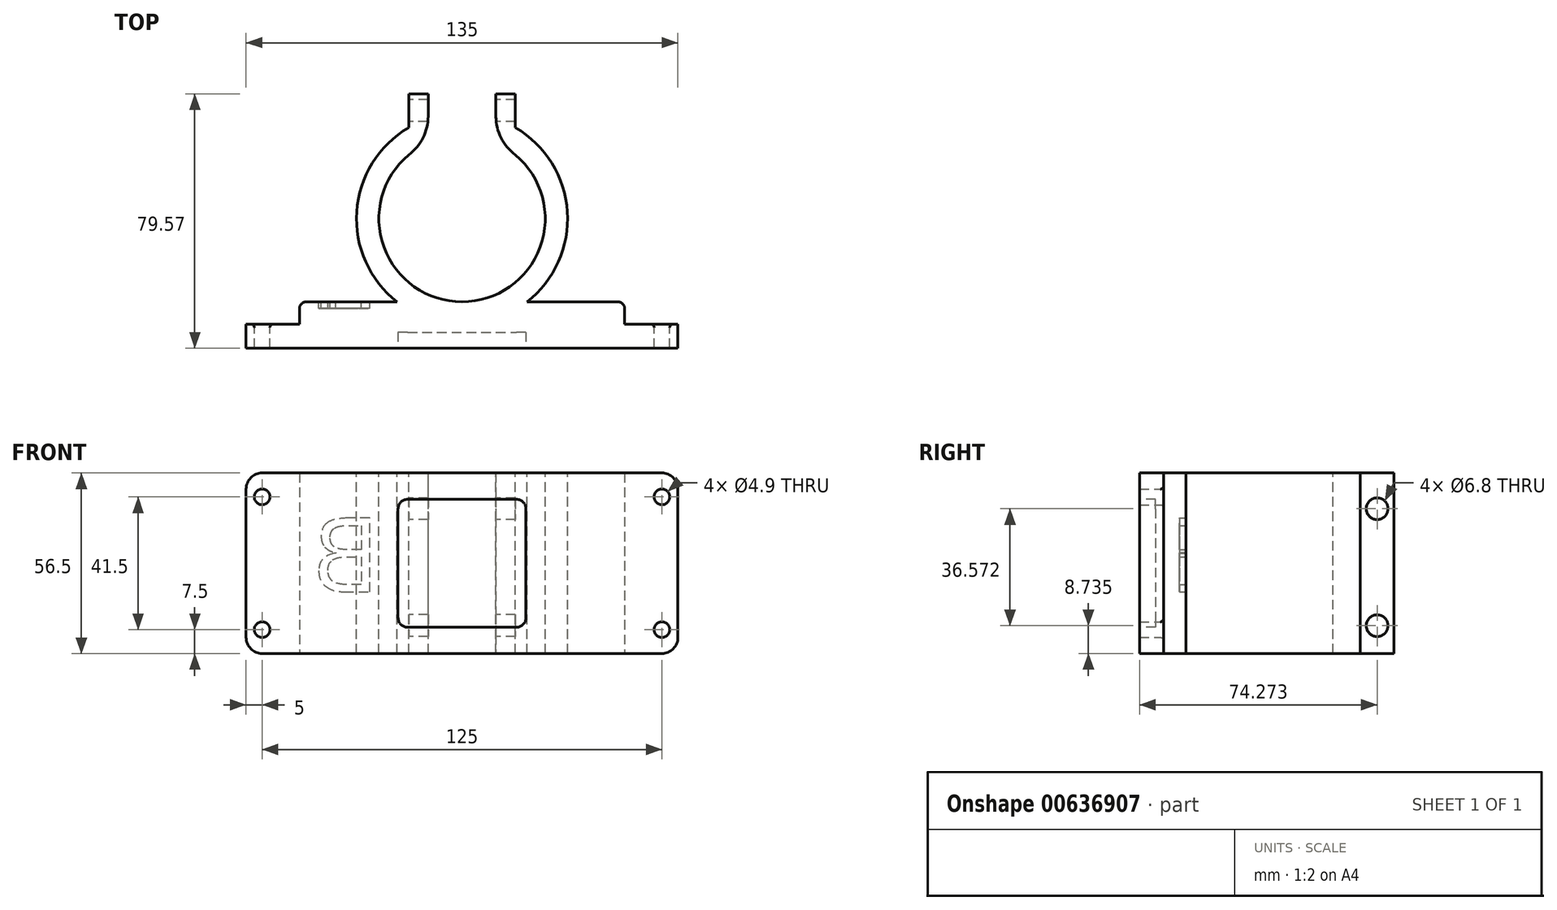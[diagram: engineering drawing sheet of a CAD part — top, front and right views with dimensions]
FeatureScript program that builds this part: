
annotation { "Feature Type Name" : "Feature", "Feature Type Description" : "" }
export const myFeature = defineFeature(function(context is Context, id is Id, definition is map)
    precondition{}
    {
        {
            var Q0;
            Q0=qCreatedBy(makeId("Front.planeOp"),FACE);
            var sketch = newSketch(context, id + "F0", { "sketchPlane" : qUnion([Q0])});
            skLineSegment(sketch, "E0.bottom", {"start": v(67.5, -28.25) * mm, "end": v(-67.5, -28.25) * mm});
            skLineSegment(sketch, "E0.top", {"start": v(67.5, 28.25) * mm, "end": v(-67.5, 28.25) * mm});
            skLineSegment(sketch, "E0.left", {"start": v(67.5, -28.25) * mm, "end": v(67.5, 28.25) * mm});
            skLineSegment(sketch, "E0.right", {"start": v(-67.5, -28.25) * mm, "end": v(-67.5, 28.25) * mm});
            skPoint(sketch, "E0.middle", {"position": v(0, 0) * mm});
            skCircle(sketch, "E1", {"center": v(-62.5, 20.75) * mm, "radius": 2.45 * mm});
            skCircle(sketch, "E2", {"center": v(-62.5, -20.75) * mm, "radius": 2.45 * mm});
            skCircle(sketch, "E3", {"center": v(62.5, 20.75) * mm, "radius": 2.45 * mm});
            skCircle(sketch, "E4", {"center": v(62.5, -20.75) * mm, "radius": 2.45 * mm});
            skLineSegment(sketch, "E5", {"start": v(-62.5, 20.75) * mm, "end": v(-62.5, -20.75) * mm});
            skLineSegment(sketch, "E6", {"start": v(-62.5, -20.75) * mm, "end": v(62.5, -20.75) * mm});
            skLineSegment(sketch, "E7", {"start": v(62.5, -20.75) * mm, "end": v(62.5, 20.75) * mm});
            skLineSegment(sketch, "E8", {"start": v(-62.5, 20.75) * mm, "end": v(62.5, 20.75) * mm});
            skLineSegment(sketch, "E9", {"start": v(-62.5, 20.75) * mm, "end": v(-62.5, 28.25) * mm});
            skLineSegment(sketch, "E10", {"start": v(-62.5, -20.75) * mm, "end": v(-62.5, -28.25) * mm});
            skLineSegment(sketch, "E11", {"start": v(62.5, 20.75) * mm, "end": v(67.5, 20.75) * mm});
            skLineSegment(sketch, "E12", {"start": v(-62.5, 20.75) * mm, "end": v(-67.5, 20.75) * mm});
            skSolve(sketch);
        }
        {
            var Q0;
            {var subQ9=sQuery(id+"F0.wireOp",EDGE,"E0.left");var subQ11=sQuery(id+"F0.wireOp",EDGE,"E0.top");var subQ12=makeQuery(id+"F0.imprint","INTERSECT",VERTEX,{"derivedFrom":[subQ11,subQ9]});Q0=makeQuery(id+"F0.imprint","IMPRINT",FACE,{"disambiguationData":[TD([[makeQuery(id+"F0.imprint","IMPRINT",EDGE,{"disambiguationData":[TD([[subQ12,-1.0]])],"derivedFrom":subQ11}),1.0]])]});}
            var Q1;
            {var subQ5=sQuery(id+"F0.wireOp",EDGE,"E0.right");var subQ6=sQuery(id+"F0.wireOp",EDGE,"E0.top");var subQ7=makeQuery(id+"F0.imprint","INTERSECT",VERTEX,{"derivedFrom":[subQ6,subQ5]});Q1=makeQuery(id+"F0.imprint","IMPRINT",FACE,{"disambiguationData":[TD([[makeQuery(id+"F0.imprint","IMPRINT",EDGE,{"disambiguationData":[TD([[subQ7,1.0]])],"derivedFrom":subQ6}),1.0]])]});}
            var Q2;
            {var subQ5=sQuery(id+"F0.wireOp",EDGE,"E0.bottom");var subQ11=sQuery(id+"F0.wireOp",EDGE,"E0.right");var subQ12=makeQuery(id+"F0.imprint","INTERSECT",VERTEX,{"derivedFrom":[subQ5,subQ11]});Q2=makeQuery(id+"F0.imprint","IMPRINT",FACE,{"disambiguationData":[TD([[makeQuery(id+"F0.imprint","IMPRINT",EDGE,{"disambiguationData":[TD([[subQ12,1.0]])],"derivedFrom":subQ5}),-1.0]])]});}
            var Q3;
            {var subQ9=sQuery(id+"F0.wireOp",EDGE,"E8");var subQ13=sQuery(id+"F0.wireOp",EDGE,"E1");var subQ14=makeQuery(id+"F0.imprint","INTERSECT",VERTEX,{"derivedFrom":[subQ13,subQ9]});Q3=makeQuery(id+"F0.imprint","IMPRINT",FACE,{"disambiguationData":[TD([[makeQuery(id+"F0.imprint","IMPRINT",EDGE,{"disambiguationData":[TD([[subQ14,1.0]])],"derivedFrom":subQ13}),-1.0]])]});}
            var Q4;
            {var subQ10=sQuery(id+"F0.wireOp",EDGE,"E0.left");var subQ11=sQuery(id+"F0.wireOp",EDGE,"E0.bottom");var subQ12=makeQuery(id+"F0.imprint","INTERSECT",VERTEX,{"derivedFrom":[subQ11,subQ10]});Q4=makeQuery(id+"F0.imprint","IMPRINT",FACE,{"disambiguationData":[TD([[makeQuery(id+"F0.imprint","IMPRINT",EDGE,{"disambiguationData":[TD([[subQ12,-1.0]])],"derivedFrom":subQ11}),-1.0]])]});}
            extrude(context, id + "F1", {"entities" : qUnion([Q0, Q1, Q2, Q3, Q4]), "depth" : 7.5 * mm, "offsetDistance" : 25.4 * mm});
        }
        {
            var Q0;
            Q0=makeQuery(id+"F1.opExtrude","SWEPT_EDGE",EDGE,{"disambiguationData":[OSD([sQuery(id+"F0.wireOp",EDGE,"E0.top"),sQuery(id+"F0.wireOp",EDGE,"E0.left")])]});
            var Q1;
            Q1=makeQuery(id+"F1.opExtrude","SWEPT_EDGE",EDGE,{"disambiguationData":[OSD([sQuery(id+"F0.wireOp",EDGE,"E0.bottom"),sQuery(id+"F0.wireOp",EDGE,"E0.left")])]});
            var Q2;
            Q2=makeQuery(id+"F1.opExtrude","SWEPT_EDGE",EDGE,{"disambiguationData":[OSD([sQuery(id+"F0.wireOp",EDGE,"E0.bottom"),sQuery(id+"F0.wireOp",EDGE,"E0.right")])]});
            var Q3;
            Q3=makeQuery(id+"F1.opExtrude","SWEPT_EDGE",EDGE,{"disambiguationData":[OSD([sQuery(id+"F0.wireOp",EDGE,"E0.top"),sQuery(id+"F0.wireOp",EDGE,"E0.right")])]});
            fillet(context, id + "F2", {"entities" : qUnion([Q0, Q1, Q2, Q3]), "radius" : 5.08 * mm, "tangentPropagation" : true, "allowEdgeOverflow" : false});
        }
        {
            var Q0;
            Q0=makeQuery(id+"F1.opExtrude","SWEPT_FACE",FACE,{"disambiguationData":[OSD([sQuery(id+"F0.wireOp",EDGE,"E0.top")])]});
            var sketch = newSketch(context, id + "F3", { "sketchPlane" : qUnion([Q0])});
            skArc(sketch, "E13", {"start": v(-16.68, 52.94) * mm, "mid": v(0, 7) * mm, "end": v(16.68, 52.94) * mm});
            skArc(sketch, "E14", {"start": v(-16.68, 61.47) * mm, "mid": v(0, 0) * mm, "end": v(16.68, 61.47) * mm});
            skLineSegment(sketch, "E15.left", {"start": v(16.68, 52.94) * mm, "end": v(16.68, 72.07) * mm});
            skLineSegment(sketch, "E15.right", {"start": v(-16.68, 52.94) * mm, "end": v(-16.68, 72.07) * mm});
            skPoint(sketch, "E15.middle", {"position": v(0, 59) * mm});
            skPoint(sketch, "E15.bottom.end.orphan", {"position": v(-16.68, 45.93) * mm});
            skPoint(sketch, "E16.orphan", {"position": v(16.68, 45.93) * mm});
            skLineSegment(sketch, "E17", {"start": v(-16.68, 72.07) * mm, "end": v(-10.6, 72.07) * mm});
            skLineSegment(sketch, "E18", {"start": v(-10.6, 72.07) * mm, "end": v(-10.6, 52.94) * mm});
            skLineSegment(sketch, "E19", {"start": v(-10.6, 52.94) * mm, "end": v(-16.68, 52.94) * mm});
            skLineSegment(sketch, "E20", {"start": v(16.68, 72.07) * mm, "end": v(10.6, 72.07) * mm});
            skLineSegment(sketch, "E21", {"start": v(10.6, 72.07) * mm, "end": v(10.6, 52.94) * mm});
            skLineSegment(sketch, "E22", {"start": v(10.6, 52.94) * mm, "end": v(16.68, 52.94) * mm});
            skSolve(sketch);
        }
        {
            var Q0;
            Q0 = qSketchRegion(id + "F3", true);
            extrude(context, id + "F4", {"entities" : qUnion([Q0]), "oppositeDirection" : true, "depth" : 56.5 * mm, "offsetDistance" : 25.4 * mm});
        }
        {
            var Q0;
            Q0=makeQuery(id+"F4.opExtrude","SWEPT_EDGE",EDGE,{"disambiguationData":[OSD([sQuery(id+"F3.wireOp",EDGE,"E18"),sQuery(id+"F3.wireOp",EDGE,"E19")])]});
            var Q1;
            Q1=makeQuery(id+"F4.opExtrude","SWEPT_EDGE",EDGE,{"disambiguationData":[OSD([sQuery(id+"F3.wireOp",EDGE,"E21"),sQuery(id+"F3.wireOp",EDGE,"E22")])]});
            fillet(context, id + "F5", {"entities" : qUnion([Q0, Q1]), "radius" : 15 * mm, "tangentPropagation" : true, "allowEdgeOverflow" : false});
        }
        {
            var Q0;
            Q0=makeQuery(id+"F4.opExtrude","SWEPT_FACE",FACE,{"disambiguationData":[OSD([sQuery(id+"F3.wireOp",EDGE,"E15.right")])]});
            var sketch = newSketch(context, id + "F6", { "sketchPlane" : qUnion([Q0])});
            skCircle(sketch, "E23", {"center": v(-66.77, -19.51) * mm, "radius": 3.4 * mm});
            skCircle(sketch, "E24", {"center": v(-66.77, 17.06) * mm, "radius": 3.4 * mm});
            skPoint(sketch, "E24.centerSnap0", {"position": v(-66.77, 28.25) * mm});
            skLineSegment(sketch, "E25", {"start": v(-66.77, -19.51) * mm, "end": v(-66.77, 17.06) * mm});
            skSolve(sketch);
        }
        {
            var Q0;
            Q0=makeQuery(id+"F6.imprint","IMPRINT",FACE,{"disambiguationData":[TD([[makeQuery(id+"F6.imprint","IMPRINT",EDGE,{"derivedFrom":sQuery(id+"F6.wireOp",EDGE,"E23")}),1.0]])]});
            var Q1;
            Q1=makeQuery(id+"F6.imprint","IMPRINT",FACE,{"disambiguationData":[TD([[makeQuery(id+"F6.imprint","IMPRINT",EDGE,{"derivedFrom":sQuery(id+"F6.wireOp",EDGE,"E24")}),1.0]])]});
            extrude(context, id + "F7", {"entities" : qUnion([Q0, Q1]), "operationType" : NewBodyOperationType.REMOVE, "oppositeDirection" : true, "depth" : 37.85 * mm, "offsetDistance" : 25.4 * mm});
        }
        {
            var Q0;
            Q0=makeQuery(id+"F1.opExtrude","SWEPT_FACE",FACE,{"disambiguationData":[OSD([sQuery(id+"F0.wireOp",EDGE,"E0.bottom")])]});
            var sketch = newSketch(context, id + "F8", { "sketchPlane" : qUnion([Q0])});
            skLineSegment(sketch, "E26.bottom", {"start": v(-50.8, 0) * mm, "end": v(50.8, 0) * mm});
            skLineSegment(sketch, "E26.top", {"start": v(-50.8, -7) * mm, "end": v(50.8, -7) * mm});
            skLineSegment(sketch, "E26.left", {"start": v(-50.8, 0) * mm, "end": v(-50.8, -7) * mm});
            skLineSegment(sketch, "E26.right", {"start": v(50.8, 0) * mm, "end": v(50.8, -7) * mm});
            skLineSegment(sketch, "E27", {"start": v(-62.42, 0) * mm, "end": v(-50.8, 0) * mm});
            skLineSegment(sketch, "E28", {"start": v(50.8, 0) * mm, "end": v(62.42, 0) * mm});
            skSolve(sketch);
        }
        {
            var Q0;
            Q0=makeQuery(id+"F8.imprint","IMPRINT",FACE,{"disambiguationData":[TD([[makeQuery(id+"F8.imprint","IMPRINT",EDGE,{"derivedFrom":sQuery(id+"F8.wireOp",EDGE,"E26.bottom")}),1.0]])]});
            extrude(context, id + "F9", {"entities" : qUnion([Q0]), "operationType" : NewBodyOperationType.ADD, "oppositeDirection" : true, "depth" : 56.5 * mm, "offsetDistance" : 25.4 * mm});
        }
        {
            var Q0;
            Q0=makeQuery(id+"F9.opExtrude","SWEPT_EDGE",EDGE,{"disambiguationData":[OSD([sQuery(id+"F8.wireOp",EDGE,"E26.top"),sQuery(id+"F8.wireOp",EDGE,"E26.left")])]});
            var Q1;
            Q1=makeQuery(id+"F9.opExtrude","SWEPT_EDGE",EDGE,{"disambiguationData":[OSD([sQuery(id+"F8.wireOp",EDGE,"E26.top"),sQuery(id+"F8.wireOp",EDGE,"E26.right")])]});
            fillet(context, id + "F10", {"entities" : qUnion([Q0, Q1]), "radius" : 2 * mm, "tangentPropagation" : true, "allowEdgeOverflow" : false});
        }
        {
            var Q0;
            Q0=makeQuery(id+"F1.opExtrude","CAP_FACE",FACE,{"disambiguationData":[OSD([sQuery(id+"F0.wireOp",EDGE,"E0.bottom"),sQuery(id+"F0.wireOp",EDGE,"E0.top"),sQuery(id+"F0.wireOp",EDGE,"E0.left"),sQuery(id+"F0.wireOp",EDGE,"E0.right"),sQuery(id+"F0.wireOp",EDGE,"E1"),sQuery(id+"F0.wireOp",EDGE,"E2"),sQuery(id+"F0.wireOp",EDGE,"E3"),sQuery(id+"F0.wireOp",EDGE,"E4")])],"isStart":false});
            var sketch = newSketch(context, id + "F11", { "sketchPlane" : qUnion([Q0])});
            skLineSegment(sketch, "E29.bottom", {"start": v(-17, 20) * mm, "end": v(17, 20) * mm});
            skLineSegment(sketch, "E29.top", {"start": v(-17, -20) * mm, "end": v(17, -20) * mm});
            skLineSegment(sketch, "E29.left", {"start": v(-20, 17) * mm, "end": v(-20, -17) * mm});
            skLineSegment(sketch, "E29.right", {"start": v(20, 17) * mm, "end": v(20, -17) * mm});
            skPoint(sketch, "E29.middle", {"position": v(0, 0) * mm});
            skPoint(sketch, "E30.visualSharp", {"position": v(-20, 20) * mm});
            skArc(sketch, "E30.filletArc", {"start": v(-17, 20) * mm, "mid": v(-19.12, 19.12) * mm, "end": v(-20, 17) * mm});
            skPoint(sketch, "E31.visualSharp", {"position": v(20, 20) * mm});
            skArc(sketch, "E31.filletArc", {"start": v(20, 17) * mm, "mid": v(19.12, 19.12) * mm, "end": v(17, 20) * mm});
            skPoint(sketch, "E32.visualSharp", {"position": v(20, -20) * mm});
            skArc(sketch, "E32.filletArc", {"start": v(17, -20) * mm, "mid": v(19.12, -19.12) * mm, "end": v(20, -17) * mm});
            skPoint(sketch, "E33.visualSharp", {"position": v(-20, -20) * mm});
            skArc(sketch, "E33.filletArc", {"start": v(-20, -17) * mm, "mid": v(-19.12, -19.12) * mm, "end": v(-17, -20) * mm});
            skSolve(sketch);
        }
        {
            var Q0;
            Q0=makeQuery(id+"F11.imprint","IMPRINT",FACE,{"disambiguationData":[TD([[makeQuery(id+"F11.imprint","IMPRINT",EDGE,{"derivedFrom":sQuery(id+"F11.wireOp",EDGE,"E29.bottom")}),-1.0]])]});
            extrude(context, id + "F12", {"entities" : qUnion([Q0]), "operationType" : NewBodyOperationType.REMOVE, "oppositeDirection" : true, "depth" : 5 * mm, "offsetDistance" : 25.4 * mm});
        }
        {
            var Q0;
            Q0=makeQuery(id+"F1.opExtrude","CAP_EDGE",EDGE,{"disambiguationData":[OSD([sQuery(id+"F0.wireOp",EDGE,"E2")])],"isStart":true});
            var Q1;
            Q1=makeQuery(id+"F1.opExtrude","CAP_EDGE",EDGE,{"disambiguationData":[OSD([sQuery(id+"F0.wireOp",EDGE,"E1")])],"isStart":true});
            var Q2;
            Q2=makeQuery(id+"F1.opExtrude","CAP_EDGE",EDGE,{"disambiguationData":[OSD([sQuery(id+"F0.wireOp",EDGE,"E3")])],"isStart":true});
            var Q3;
            Q3=makeQuery(id+"F1.opExtrude","CAP_EDGE",EDGE,{"disambiguationData":[OSD([sQuery(id+"F0.wireOp",EDGE,"E4")])],"isStart":true});
            fillet(context, id + "F13", {"entities" : qUnion([Q0, Q1, Q2, Q3]), "radius" : 1 * mm, "tangentPropagation" : true, "allowEdgeOverflow" : false});
        }
        {
            var Q0;
            {var subQ1=sQuery(id+"F8.wireOp",EDGE,"E26.left");var subQ2=sQuery(id+"F8.wireOp",EDGE,"E26.top");Q0=makeQuery(id+"F9.boolean.opBoolean","SPLIT",FACE,{"disambiguationData":[TD([makeQuery(id+"F9.opExtrude","SWEPT_FACE",FACE,{"disambiguationData":[OSD([subQ1])]})])],"derivedFrom":makeQuery(id+"F9.opExtrude","SWEPT_FACE",FACE,{"disambiguationData":[OSD([subQ2])]})});}
            var sketch = newSketch(context, id + "F14", { "sketchPlane" : qUnion([Q0])});
            skText(sketch, "E34", { "text": "B", "fontName": "OpenSans-Regular.ttf"});
            const initialGuessF14  = {"E34": [0.02565, -0.00891, 1, 0, 0.02325]};
            skSetInitialGuess(sketch, initialGuessF14);
            skSolve(sketch);
        }
        {
            var Q0;
            Q0 = qSketchRegion(id + "F14", true);
            extrude(context, id + "F15", {"entities" : qUnion([Q0]), "operationType" : NewBodyOperationType.REMOVE, "oppositeDirection" : true, "depth" : 2 * mm, "offsetDistance" : 25.4 * mm});
        }
    });
